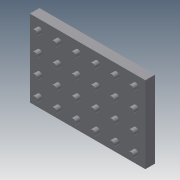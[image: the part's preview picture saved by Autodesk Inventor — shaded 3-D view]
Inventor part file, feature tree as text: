
AUTODESK INVENTOR PART (.ipt)
format: ipt  version: 2015 (Build 190159000, 159)  size: 121,344 bytes
history: native  units: in
note: dims shown in document units (in); Inventor stores cm internally (conversion verified against a paired STEP export)
features: extrude x2, sketch x2, pattern_linear x1, projected_geometry x1
ambient origin geometry x8: Origin, YZ Plane, XZ Plane, XY Plane, X Axis, Y Axis, Z Axis, Center Point
bodies: Solid1 (feature_tree)
feature tree (6):
  extrude  "Extrusion1"  Depth=4.0in
  extrude  "Extrusion2"  Depth=0.25in
  pattern_linear  "Rectangular Pattern1"  Spacing1=0.5in  [1 undecoded]
  sketch  "Sketch1"  dims[d0=6.0in d1=4.0in]
  sketch  "Sketch2"  dims[d2=0.5in d3=0.0in d4=0.3in d5=0.5in d6=0.5in d7=0.25in d8=0.0in d9=1.5748in d11=1.0in d12=2.3622in d14=1.0in]
  projected_geometry  "Projected Loop1"
note: 1 required parameter value undecoded (feature->parameter linkage not recoverable at this tier; creation-order binding heuristic only, values carry confidence <= 0.55)
